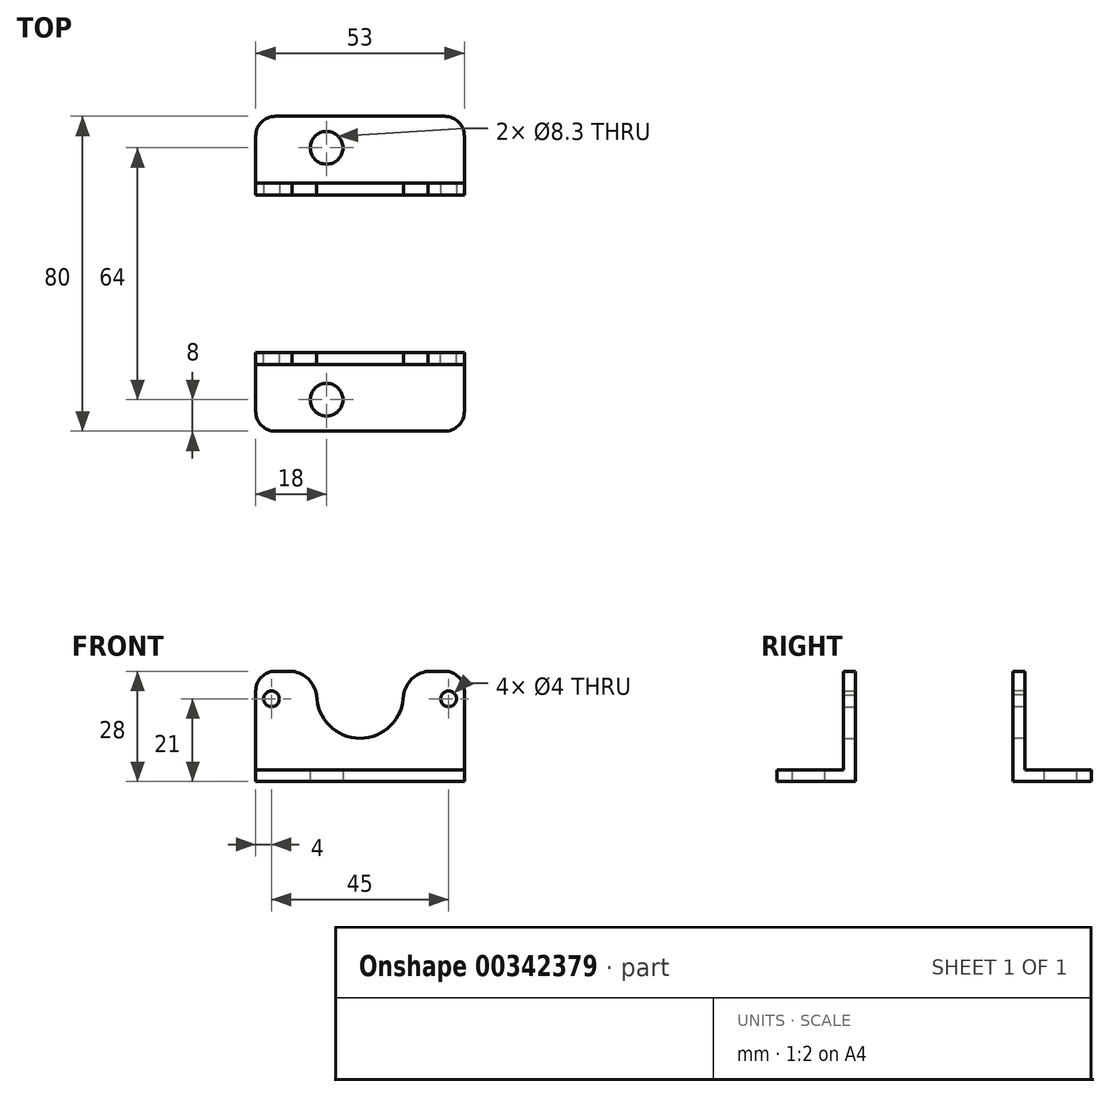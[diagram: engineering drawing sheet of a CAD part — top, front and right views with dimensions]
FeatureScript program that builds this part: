
annotation { "Feature Type Name" : "Feature", "Feature Type Description" : "" }
export const myFeature = defineFeature(function(context is Context, id is Id, definition is map)
    precondition{}
    {
        {
            var Q0;
            Q0=qCreatedBy(makeId("Top.planeOp"),FACE);
            var sketch = newSketch(context, id + "F0", { "sketchPlane" : qUnion([Q0])});
            skLineSegment(sketch, "E0.bottom", {"start": v(-26.5, 10) * mm, "end": v(26.5, 10) * mm});
            skLineSegment(sketch, "E0.top", {"start": v(-26.5, -10) * mm, "end": v(26.5, -10) * mm});
            skLineSegment(sketch, "E0.left", {"start": v(-26.5, 10) * mm, "end": v(-26.5, -10) * mm});
            skLineSegment(sketch, "E0.right", {"start": v(26.5, 10) * mm, "end": v(26.5, -10) * mm});
            skPoint(sketch, "E0.middle", {"position": v(0, 0) * mm});
            skCircle(sketch, "E1", {"center": v(-8.5, 2) * mm, "radius": 4.15 * mm});
            skSolve(sketch);
        }
        {
            var Q0;
            Q0=makeQuery(id+"F0.imprint","IMPRINT",FACE,{"disambiguationData":[TD([[makeQuery(id+"F0.imprint","IMPRINT",EDGE,{"derivedFrom":sQuery(id+"F0.wireOp",EDGE,"E0.bottom")}),-1.0]])]});
            extrude(context, id + "F1", {"entities" : qUnion([Q0]), "depth" : 3 * mm});
        }
        {
            var Q0;
            Q0=makeQuery(id+"F1.opExtrude","SWEPT_EDGE",EDGE,{"disambiguationData":[OSD([sQuery(id+"F0.wireOp",EDGE,"E0.bottom"),sQuery(id+"F0.wireOp",EDGE,"E0.left")])]});
            var Q1;
            Q1=makeQuery(id+"F1.opExtrude","SWEPT_EDGE",EDGE,{"disambiguationData":[OSD([sQuery(id+"F0.wireOp",EDGE,"E0.bottom"),sQuery(id+"F0.wireOp",EDGE,"E0.right")])]});
            fillet(context, id + "F2", {"entities" : qUnion([Q0, Q1]), "radius" : 5 * mm, "tangentPropagation" : true, "allowEdgeOverflow" : false});
        }
        {
            var Q0;
            Q0=makeQuery(id+"F1.opExtrude","SWEPT_FACE",FACE,{"disambiguationData":[OSD([sQuery(id+"F0.wireOp",EDGE,"E0.top")])]});
            var sketch = newSketch(context, id + "F3", { "sketchPlane" : qUnion([Q0])});
            skLineSegment(sketch, "E2.bottom", {"start": v(-26.5, 0) * mm, "end": v(26.5, 0) * mm});
            skLineSegment(sketch, "E2.top", {"start": v(-26.5, 28) * mm, "end": v(-17.23, 28) * mm});
            skLineSegment(sketch, "E2.left", {"start": v(-26.5, 0) * mm, "end": v(-26.5, 28) * mm});
            skLineSegment(sketch, "E2.right", {"start": v(26.5, 0) * mm, "end": v(26.5, 28) * mm});
            skLineSegment(sketch, "E3", {"start": v(-35.78, 21) * mm, "end": v(42.94, 21) * mm, "construction": true});
            skCircle(sketch, "E4", {"center": v(-22.5, 21) * mm, "radius": 2 * mm});
            skCircle(sketch, "E5.MirrorC", {"center": v(22.5, 21) * mm, "radius": 2 * mm});
            skLineSegment(sketch, "E6", {"start": v(-36.12, 22) * mm, "end": v(31.18, 22) * mm, "construction": true});
            skArc(sketch, "E7", {"start": v(-11, 22) * mm, "mid": v(0, 11) * mm, "end": v(11, 22) * mm});
            skPoint(sketch, "E7.centerSnap0", {"position": v(0, 28) * mm});
            skArc(sketch, "E8", {"start": v(-25.5, 22) * mm, "mid": v(-25.57, 21.5) * mm, "end": v(-25.6, 21) * mm});
            skPoint(sketch, "E8.first.point", {"position": v(-11, 22) * mm});
            skPoint(sketch, "E8.second.point", {"position": v(-19.27, 28) * mm});
            skPoint(sketch, "E8.third.point", {"position": v(-17.23, 28) * mm});
            skArc(sketch, "E9.MirrorC", {"start": v(25.5, 22) * mm, "mid": v(25.57, 21.5) * mm, "end": v(25.6, 21) * mm});
            skArc(sketch, "E10.trimOffspring", {"start": v(-10.9, 20.45) * mm, "mid": v(-13.32, 26.18) * mm, "end": v(-19.27, 28) * mm});
            skLineSegment(sketch, "E11.trimOffspring", {"start": v(17.23, 28) * mm, "end": v(26.5, 28) * mm});
            skArc(sketch, "E12.trimOffspring", {"start": v(10.9, 20.45) * mm, "mid": v(13.32, 26.18) * mm, "end": v(19.27, 28) * mm});
            skSolve(sketch);
        }
        {
            var Q0;
            Q0=makeQuery(id+"F3.imprint","IMPRINT",FACE,{"disambiguationData":[TD([[makeQuery(id+"F3.imprint","IMPRINT",EDGE,{"derivedFrom":sQuery(id+"F3.wireOp",EDGE,"E4")}),-1.0]])]});
            extrude(context, id + "F4", {"entities" : qUnion([Q0]), "operationType" : NewBodyOperationType.ADD, "oppositeDirection" : true, "depth" : 3 * mm});
        }
        {
            var Q0;
            Q0=makeQuery(id+"F4.opExtrude","SWEPT_EDGE",EDGE,{"disambiguationData":[OSD([sQuery(id+"F3.wireOp",EDGE,"E2.top"),sQuery(id+"F3.wireOp",EDGE,"E2.left")])]});
            var Q1;
            Q1=makeQuery(id+"F4.opExtrude","SWEPT_EDGE",EDGE,{"disambiguationData":[OSD([sQuery(id+"F3.wireOp",EDGE,"E2.right"),sQuery(id+"F3.wireOp",EDGE,"E11.trimOffspring")])]});
            fillet(context, id + "F5", {"entities" : qUnion([Q0, Q1]), "radius" : 5 * mm, "tangentPropagation" : true, "allowEdgeOverflow" : false});
        }
        {
            var Q0;
            Q0=qCreatedBy(makeId("Front.planeOp"),FACE);
            cPlane(context, id + "F6", {"entities" : qUnion([Q0]), "cplaneType" : CPlaneType.OFFSET, "offset" : 30 * mm, "width" : 150 * mm, "height" : 150 * mm});
        }
        {
            var Q0;
            Q0=makeQuery(id+"F1.opExtrude","SWEPT_BODY",BODY,{"disambiguationData":[OSD([sQuery(id+"F0.wireOp",EDGE,"E0.bottom"),sQuery(id+"F0.wireOp",EDGE,"E0.top"),sQuery(id+"F0.wireOp",EDGE,"E0.left"),sQuery(id+"F0.wireOp",EDGE,"E0.right"),sQuery(id+"F0.wireOp",EDGE,"E1")])]});
            var Q1;
            Q1=qCreatedBy(id+"F6.planeOp",FACE);
            mirror(context, id + "F7", {"entities" : qUnion([Q0]), "mirrorPlane" : qUnion([Q1])});
        }
    });
